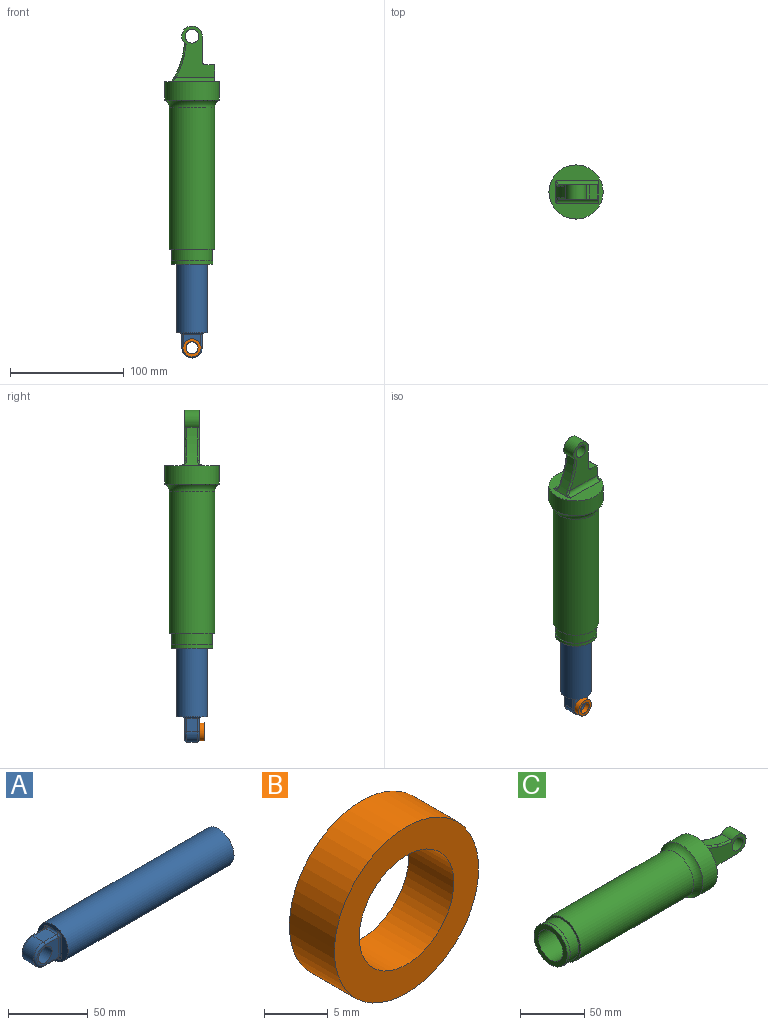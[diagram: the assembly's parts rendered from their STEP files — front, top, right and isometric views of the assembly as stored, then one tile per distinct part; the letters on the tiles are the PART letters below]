
ASSEMBLY  parts=3 mates=2
PART A: 23 faces, bbox 169.7x27x27 mm
  f0: plane 27x27mm, normal (-1,0,0), area 254.8mm2, adj f1,f14,f15,f16,f17,f18,f19,f20
  f1: cylinder r=13.5mm len=147mm, axis (-1,0,0), area 12469mm2, adj f0,f2
  f2: plane 27x27mm, normal (1,0,0), area 572.6mm2, adj f1
  f3: plane 11.5x9.5mm, normal (0,0,1), area 109.2mm2, adj f4,f8,f11,f14
  f4: cylinder r=9mm len=18mm, axis (0,1,0), area 268.6mm2, adj f3,f5,f9,f12
  f5: plane 11.5x9.5mm, normal (0,0,-1), area 109.2mm2, adj f4,f10,f13,f21
  f6: plane 19x15mm, normal (0,-1,0), area 147.8mm2, adj f11,f12,f13,f17,f22
  f7: plane 19x15mm, normal (0,1,0), area 147.8mm2, adj f8,f9,f10,f18,f22
  f8: cylinder r=1.5mm len=11.5mm, axis (-1,0,0), area 27.1mm2, adj f3,f7,f9,f16
  f9: torus R=7.5mm, axis (0,-1,0), area 62.6mm2, adj f4,f7,f8,f10
  f10: cylinder r=1.5mm len=11.5mm, axis (1,0,0), area 27.1mm2, adj f5,f7,f9,f20
  f11: cylinder r=1.5mm len=11.5mm, axis (1,0,0), area 27.1mm2, adj f3,f6,f12,f15
  f12: torus R=7.5mm, axis (0,-1,0), area 62.6mm2, adj f4,f6,f11,f13
  f13: cylinder r=1.5mm len=11.5mm, axis (-1,0,0), area 27.1mm2, adj f5,f6,f12,f19
  f14: cylinder r=1.5mm len=9.5mm, axis (0,-1,0), area 22.4mm2, adj f0,f3,f15,f16
  f15: torus R=3mm, axis (-1,0,0), area 7.6mm2, adj f0,f11,f14,f17
  f16: torus R=3mm, axis (-1,0,0), area 7.6mm2, adj f0,f8,f14,f18
  f17: cylinder r=1.5mm len=15mm, axis (0,0,-1), area 35.3mm2, adj f0,f6,f15,f19
  f18: cylinder r=1.5mm len=15mm, axis (0,0,1), area 35.3mm2, adj f0,f7,f16,f20
  f19: torus R=3mm, axis (-1,0,0), area 7.6mm2, adj f0,f13,f17,f21
  f20: torus R=3mm, axis (-1,0,0), area 7.6mm2, adj f0,f10,f18,f21
  f21: cylinder r=1.5mm len=9.5mm, axis (0,1,0), area 22.4mm2, adj f0,f5,f19,f20
  f22: cylinder r=6mm len=12.5mm, axis (0,-1,0), area 471.2mm2, adj f6,f7
PART B: 4 faces, bbox 16x5x16 mm
  f0: cylinder r=5.25mm len=10.5mm, axis (0,1,0), area 164.9mm2, adj f2,f3
  f1: cylinder r=8mm len=16mm, axis (0,1,0), area 251.3mm2, adj f2,f3
  f2: plane 16x16mm, normal (0,-1,0), area 114.5mm2, adj f0,f1
  f3: plane 16x16mm, normal (0,1,0), area 114.5mm2, adj f0,f1
PART C: 27 faces, bbox 209.2x59.8x59.8 mm
  f0: plane 22x12.5mm, normal (0,0,-1), area 275mm2, adj f12,f14,f15,f20
  f1: plane 47.72x47.72mm, normal (1,0,0), area 994.5mm2, adj f4,f13,f17,f18,f19,f22,f24
  f2: cylinder r=13.5mm len=144mm, axis (-1,0,0), area 12214.5mm2, adj f3,f11
  f3: plane 27x27mm, normal (-1,0,0), area 572.6mm2, adj f2
  f4: cylinder r=23.75mm len=47.5mm, axis (-1,0,0), area 2387.6mm2, adj f1,f5
  f5: torus R=27.51mm, axis (-1,0,0), area 1051.5mm2, adj f4,f6
  f6: cylinder r=20mm len=124.5mm, axis (-1,0,0), area 15645.1mm2, adj f5,f7
  f7: plane 40x40mm, normal (-1,0,0), area 238.8mm2, adj f6,f8
  f8: cylinder r=18mm len=36mm, axis (-1,0,0), area 1131mm2, adj f7,f9
  f9: plane 36.8x36.8mm, normal (1,0,0), area 45.7mm2, adj f8,f10
  f10: cylinder r=18.4mm len=36.8mm, axis (-1,0,0), area 346.8mm2, adj f9,f11
  f11: plane 36.8x36.8mm, normal (-1,0,0), area 491.1mm2, adj f2,f10
  f12: cylinder r=9mm len=18mm, axis (0,1,0), area 440.1mm2, adj f0,f13,f14,f15,f23,f25
  f13: cylinder r=75mm len=33.9mm, axis (0,1,0), area 358.4mm2, adj f1,f12,f22,f23,f24,f25
  f14: plane 45x33.93mm, normal (0,-1,0), area 763.4mm2, adj f0,f12,f16,f17,f19,f20,f21,f23
  f15: plane 45x33.93mm, normal (0,1,0), area 763.4mm2, adj f0,f12,f16,f17,f18,f20,f21,f25
  f16: plane 12.5x7mm, normal (1,0,0), area 87.5mm2, adj f14,f15,f20,f21
  f17: plane 20.5x14mm, normal (0,0,-1), area 181.9mm2, adj f1,f14,f15,f18,f19,f21
  f18: cylinder r=4mm len=37.18mm, axis (0,0,-1), area 223.4mm2, adj f1,f15,f17,f24
  f19: cylinder r=4mm len=37.18mm, axis (0,0,1), area 223.4mm2, adj f1,f14,f17,f22
  f20: cylinder r=3mm len=12.5mm, axis (0,-1,0), area 58.9mm2, adj f0,f14,f15,f16
  f21: cylinder r=1mm len=12.5mm, axis (0,1,0), area 19.6mm2, adj f14,f15,f16,f17
  f22: bspline ~6.7x6.17mm, area 12.9mm2, adj f1,f13,f19,f23
  f23: torus R=76.5mm, axis (0,-1,0), area 71.5mm2, adj f12,f13,f14,f22
  f24: bspline ~6.7x6.17mm, area 12.9mm2, adj f1,f13,f18,f25
  f25: torus R=76.5mm, axis (0,-1,0), area 71.5mm2, adj f12,f13,f15,f24
  f26: cylinder r=6mm len=12.5mm, axis (0,-1,0), area 471.2mm2, adj f14,f15
PLACE A rot(axis=(0,-1,0),90deg) t=(0,6.25,0)mm
PLACE B at identity fixed
PLACE C rot(axis=(0,-1,0),90deg) t=(0,6.25,-26.5)mm
MATE slider A.f1 <-> C.f2  axis (0,0,-1) through (0,6.25,86.5)mm
MATE revolute B.f0 <-> A.f4  axis (0,1,0) through (0,0,0)mm
